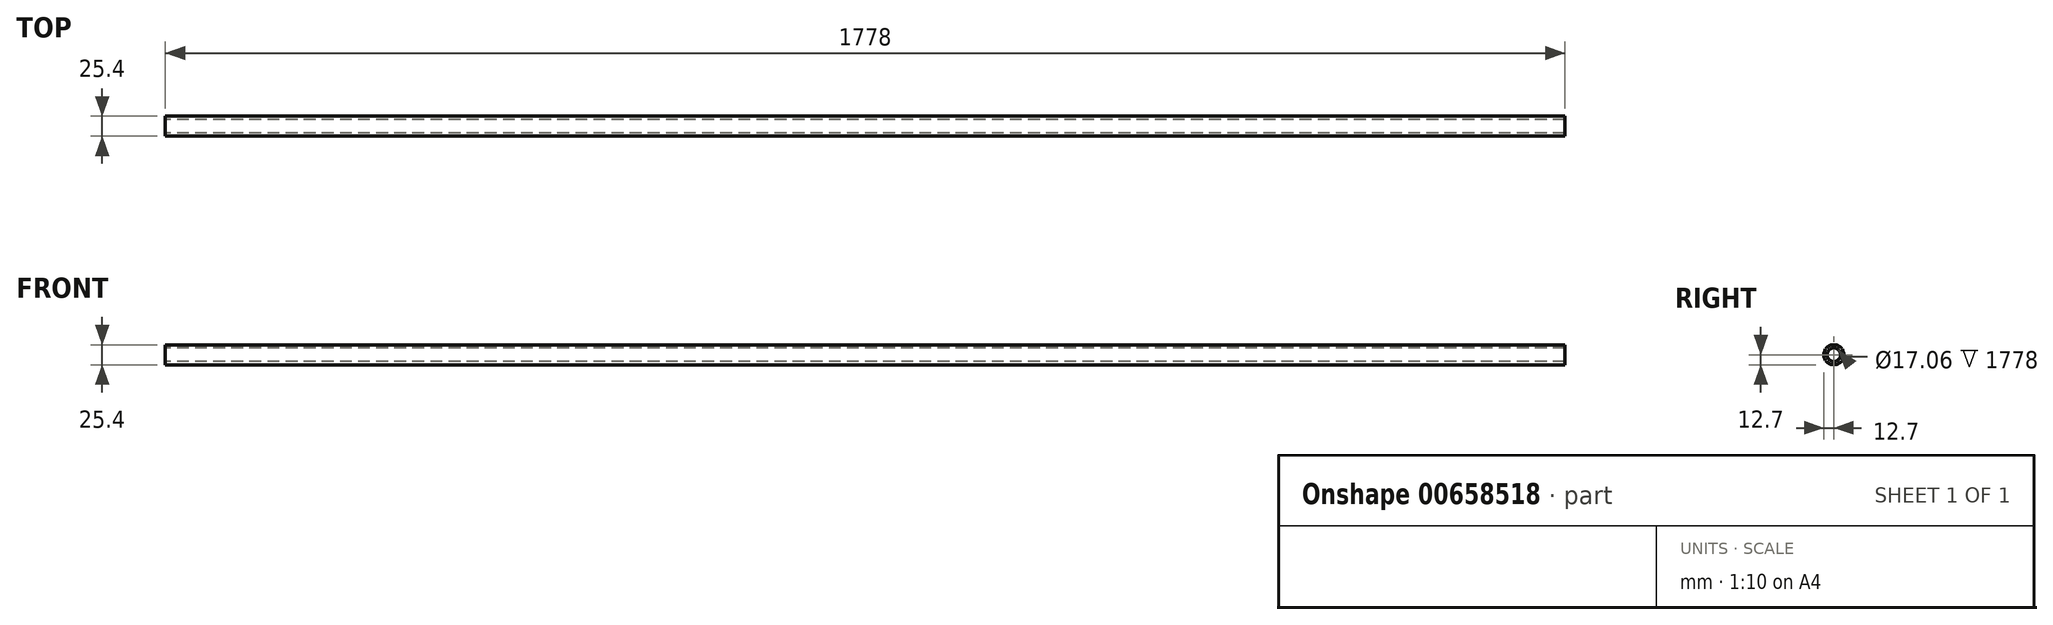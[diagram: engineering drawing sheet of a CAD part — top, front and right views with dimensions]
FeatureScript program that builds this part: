
annotation { "Feature Type Name" : "Feature", "Feature Type Description" : "" }
export const myFeature = defineFeature(function(context is Context, id is Id, definition is map)
    precondition{}
    {
        {
            var Q0;
            Q0=qCreatedBy(makeId("Right.planeOp"),FACE);
            var sketch = newSketch(context, id + "F0", { "sketchPlane" : qUnion([Q0])});
            skCircle(sketch, "E0", {"center": v(0, 0) * mm, "radius": 12.7 * mm});
            skSolve(sketch);
        }
        {
            var Q0;
            Q0=makeQuery(id+"F0.imprint","IMPRINT",FACE,{"disambiguationData":[TD([[makeQuery(id+"F0.imprint","IMPRINT",EDGE,{"derivedFrom":sQuery(id+"F0.wireOp",EDGE,"E0")}),1.0]])]});
            extrude(context, id + "F1", {"entities" : qUnion([Q0]), "depth" : 1778 * mm, "offsetDistance" : 25.4 * mm});
        }
        {
            var Q0;
            Q0=makeQuery(id+"F1.opExtrude","CAP_FACE",FACE,{"disambiguationData":[OSD([sQuery(id+"F0.wireOp",EDGE,"E0")])],"isStart":true});
            var sketch = newSketch(context, id + "F2", { "sketchPlane" : qUnion([Q0])});
            skCircle(sketch, "E1", {"center": v(0, 0) * mm, "radius": 8.53 * mm});
            skSolve(sketch);
        }
        {
            var Q0;
            Q0=makeQuery(id+"F2.imprint","IMPRINT",FACE,{"disambiguationData":[TD([[makeQuery(id+"F2.imprint","IMPRINT",EDGE,{"derivedFrom":sQuery(id+"F2.wireOp",EDGE,"E1")}),1.0]])]});
            extrude(context, id + "F3", {"entities" : qUnion([Q0]), "operationType" : NewBodyOperationType.REMOVE, "endBound" : BoundingType.THROUGH_ALL, "oppositeDirection" : true, "depth" : 25.4 * mm, "offsetDistance" : 25.4 * mm});
        }
    });
